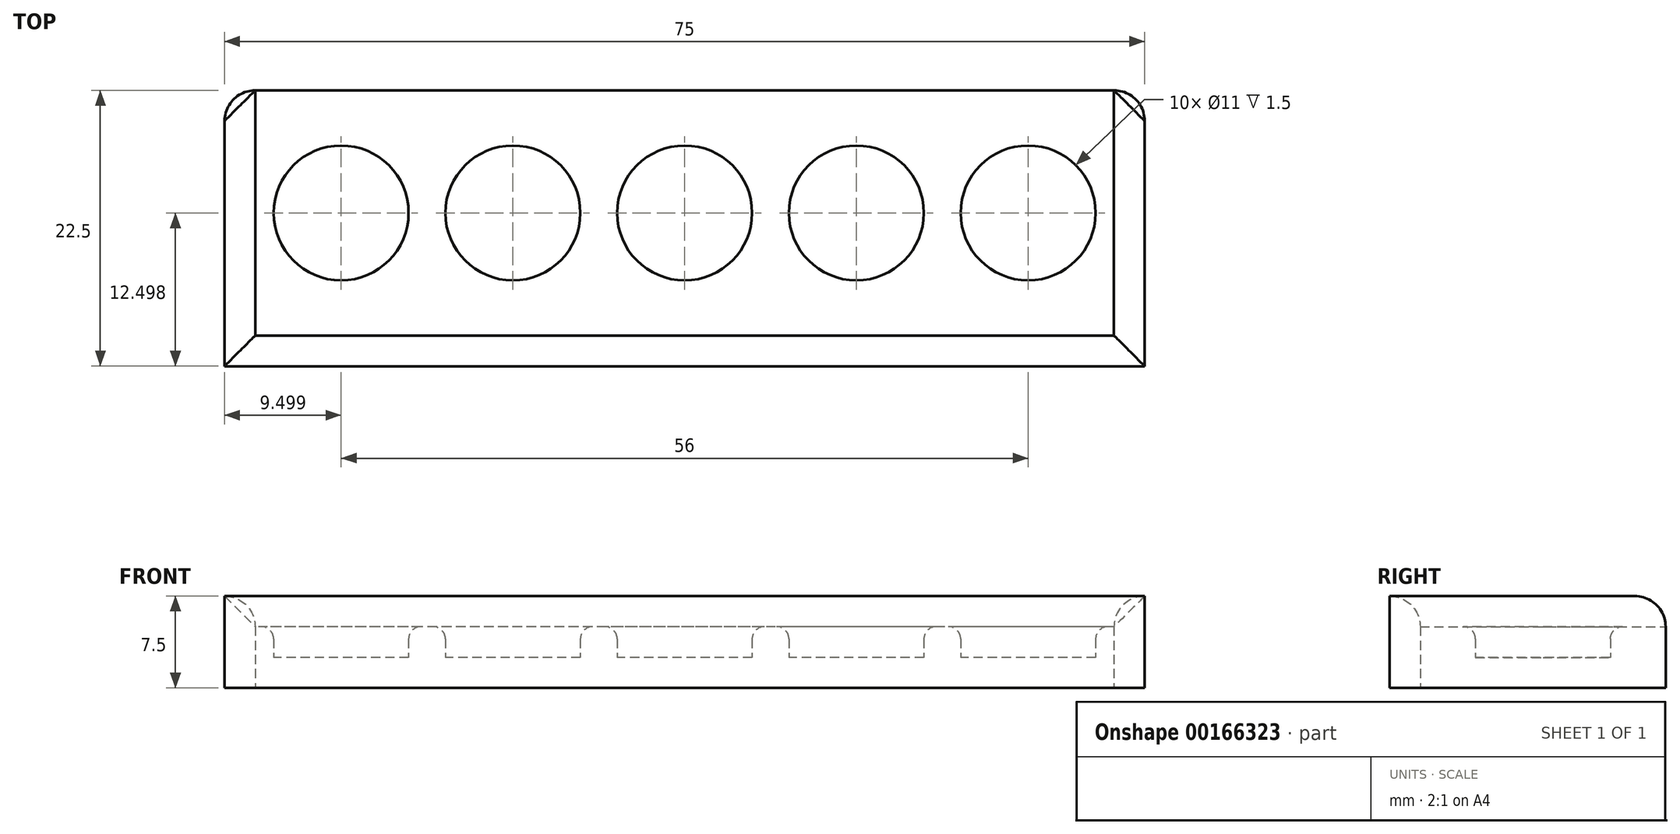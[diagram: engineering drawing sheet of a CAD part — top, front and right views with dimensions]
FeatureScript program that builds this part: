
annotation { "Feature Type Name" : "Feature", "Feature Type Description" : "" }
export const myFeature = defineFeature(function(context is Context, id is Id, definition is map)
    precondition{}
    {
        {
            var Q0;
            Q0=qCreatedBy(makeId("Top.planeOp"),FACE);
            var sketch = newSketch(context, id + "F0", { "sketchPlane" : qUnion([Q0])});
            skLineSegment(sketch, "E0.bottom", {"start": v(-145.22, 10.14) * mm, "end": v(-215.22, 10.14) * mm});
            skLineSegment(sketch, "E0.top", {"start": v(-145.22, 30.14) * mm, "end": v(-215.22, 30.14) * mm});
            skLineSegment(sketch, "E0.left", {"start": v(-145.22, 10.14) * mm, "end": v(-145.22, 30.14) * mm});
            skLineSegment(sketch, "E0.right", {"start": v(-215.22, 10.14) * mm, "end": v(-215.22, 30.14) * mm});
            skPoint(sketch, "E0.middle", {"position": v(-180.22, 20.14) * mm});
            skCircle(sketch, "E1", {"center": v(-180.22, 20.14) * mm, "radius": 5.5 * mm});
            skCircle(sketch, "E2", {"center": v(-166.22, 20.14) * mm, "radius": 5.5 * mm});
            skCircle(sketch, "E3", {"center": v(-152.22, 20.14) * mm, "radius": 5.5 * mm});
            skCircle(sketch, "E4", {"center": v(-194.22, 20.14) * mm, "radius": 5.5 * mm});
            skCircle(sketch, "E5", {"center": v(-208.22, 20.14) * mm, "radius": 5.5 * mm});
            skSolve(sketch);
        }
        {
            var Q0;
            Q0=makeQuery(id+"F0.imprint","IMPRINT",FACE,{"disambiguationData":[TD([[makeQuery(id+"F0.imprint","IMPRINT",EDGE,{"derivedFrom":sQuery(id+"F0.wireOp",EDGE,"E1")}),1.0]])]});
            var sketch = newSketch(context, id + "F1", { "sketchPlane" : qUnion([Q0])});
            skLineSegment(sketch, "E6.bottom", {"start": v(-145.22, 10.14) * mm, "end": v(-215.22, 10.14) * mm});
            skLineSegment(sketch, "E6.top", {"start": v(-145.22, 30.14) * mm, "end": v(-215.22, 30.14) * mm});
            skLineSegment(sketch, "E6.left", {"start": v(-145.22, 10.14) * mm, "end": v(-145.22, 30.14) * mm});
            skLineSegment(sketch, "E6.right", {"start": v(-215.22, 10.14) * mm, "end": v(-215.22, 30.14) * mm});
            skPoint(sketch, "E6.middle", {"position": v(-180.22, 20.14) * mm});
            skSolve(sketch);
        }
        {
            var Q0;
            Q0 = qSketchRegion(id + "F1", true);
            extrude(context, id + "F2", {"entities" : qUnion([Q0]), "depth" : 2.5 * mm, "hasSecondDirection" : true, "secondDirectionOppositeDirection" : true, "secondDirectionDepth" : 2.5 * mm});
        }
        {
            var Q0;
            Q0=makeQuery(id+"F0.imprint","IMPRINT",FACE,{"disambiguationData":[TD([[makeQuery(id+"F0.imprint","IMPRINT",EDGE,{"derivedFrom":sQuery(id+"F0.wireOp",EDGE,"E3")}),1.0]])]});
            var Q1;
            Q1=makeQuery(id+"F0.imprint","IMPRINT",FACE,{"disambiguationData":[TD([[makeQuery(id+"F0.imprint","IMPRINT",EDGE,{"derivedFrom":sQuery(id+"F0.wireOp",EDGE,"E2")}),1.0]])]});
            var Q2;
            Q2=makeQuery(id+"F0.imprint","IMPRINT",FACE,{"disambiguationData":[TD([[makeQuery(id+"F0.imprint","IMPRINT",EDGE,{"derivedFrom":sQuery(id+"F0.wireOp",EDGE,"E1")}),1.0]])]});
            var Q3;
            Q3=makeQuery(id+"F0.imprint","IMPRINT",FACE,{"disambiguationData":[TD([[makeQuery(id+"F0.imprint","IMPRINT",EDGE,{"derivedFrom":sQuery(id+"F0.wireOp",EDGE,"E4")}),1.0]])]});
            var Q4;
            Q4=makeQuery(id+"F0.imprint","IMPRINT",FACE,{"disambiguationData":[TD([[makeQuery(id+"F0.imprint","IMPRINT",EDGE,{"derivedFrom":sQuery(id+"F0.wireOp",EDGE,"E5")}),1.0]])]});
            extrude(context, id + "F3", {"entities" : qUnion([Q0, Q1, Q2, Q3, Q4]), "operationType" : NewBodyOperationType.REMOVE, "depth" : 25.4 * mm});
        }
        {
            var Q0;
            Q0=makeQuery(id+"F2.opExtrude","CAP_FACE",FACE,{"disambiguationData":[OSD([sQuery(id+"F1.wireOp",EDGE,"E6.bottom"),sQuery(id+"F1.wireOp",EDGE,"E6.top"),sQuery(id+"F1.wireOp",EDGE,"E6.left"),sQuery(id+"F1.wireOp",EDGE,"E6.right")])],"isStart":true});
            var sketch = newSketch(context, id + "F4", { "sketchPlane" : qUnion([Q0])});
            skLineSegment(sketch, "E7.bottom", {"start": v(-142.72, -30.14) * mm, "end": v(-217.72, -30.14) * mm});
            skLineSegment(sketch, "E7.top", {"start": v(-142.72, -7.64) * mm, "end": v(-217.72, -7.64) * mm});
            skLineSegment(sketch, "E7.left", {"start": v(-142.72, -30.14) * mm, "end": v(-142.72, -7.64) * mm});
            skLineSegment(sketch, "E7.right", {"start": v(-217.72, -30.14) * mm, "end": v(-217.72, -7.64) * mm});
            skSolve(sketch);
        }
        {
            var Q0;
            Q0=makeQuery(id+"F4.imprint","IMPRINT",FACE,{"disambiguationData":[TD([[makeQuery(id+"F4.imprint","IMPRINT",EDGE,{"derivedFrom":sQuery(id+"F4.wireOp",EDGE,"E7.top")}),1.0]])]});
            extrude(context, id + "F5", {"entities" : qUnion([Q0]), "oppositeDirection" : true, "depth" : 7.5 * mm});
        }
        {
            var Q0;
            Q0=makeQuery(id+"F5.opExtrude","CAP_EDGE",EDGE,{"disambiguationData":[OSD([sQuery(id+"F1.wireOp",EDGE,"E6.bottom")])],"isStart":false});
            var Q1;
            Q1=makeQuery(id+"F5.opExtrude","CAP_EDGE",EDGE,{"disambiguationData":[OSD([sQuery(id+"F1.wireOp",EDGE,"E6.left")])],"isStart":false});
            var Q2;
            Q2=makeQuery(id+"F5.opExtrude","CAP_EDGE",EDGE,{"disambiguationData":[OSD([sQuery(id+"F1.wireOp",EDGE,"E6.right")])],"isStart":false});
            var Q3;
            {var subQ0=sQuery(id+"F4.wireOp",EDGE,"E7.bottom");Q3=makeQuery(id+"F5.opExtrude","CAP_EDGE",EDGE,{"disambiguationData":[OSD([subQ0]),TDD([makeQuery(id+"F4.imprint","IMPRINT",EDGE,{"disambiguationData":[TD([[makeQuery(id+"F4.imprint","INTERSECT",VERTEX,{"derivedFrom":[makeQuery(id+"F2.opExtrude","CAP_EDGE",EDGE,{"disambiguationData":[OSD([sQuery(id+"F1.wireOp",EDGE,"E6.right")])],"isStart":true}),subQ0]}),-1.0]])],"derivedFrom":subQ0})])],"isStart":false});}
            var Q4;
            {var subQ0=sQuery(id+"F4.wireOp",EDGE,"E7.bottom");Q4=makeQuery(id+"F5.opExtrude","CAP_EDGE",EDGE,{"disambiguationData":[OSD([subQ0]),TDD([makeQuery(id+"F4.imprint","IMPRINT",EDGE,{"disambiguationData":[TD([[makeQuery(id+"F4.imprint","INTERSECT",VERTEX,{"derivedFrom":[makeQuery(id+"F2.opExtrude","CAP_EDGE",EDGE,{"disambiguationData":[OSD([sQuery(id+"F1.wireOp",EDGE,"E6.left")])],"isStart":true}),subQ0]}),1.0]])],"derivedFrom":subQ0})])],"isStart":false});}
            var Q5;
            Q5=makeQuery(id+"F5.opExtrude","SWEPT_EDGE",EDGE,{"disambiguationData":[OSD([sQuery(id+"F4.wireOp",EDGE,"E7.bottom"),sQuery(id+"F4.wireOp",EDGE,"E7.left")])]});
            var Q6;
            Q6=makeQuery(id+"F5.opExtrude","SWEPT_EDGE",EDGE,{"disambiguationData":[OSD([sQuery(id+"F4.wireOp",EDGE,"E7.bottom"),sQuery(id+"F4.wireOp",EDGE,"E7.right")])]});
            fillet(context, id + "F6", {"entities" : qUnion([Q0, Q1, Q2, Q3, Q4, Q5, Q6]), "radius" : 2.5 * mm, "tangentPropagation" : true, "allowEdgeOverflow" : false});
        }
        {
            var Q0;
            Q0=makeQuery(id+"F3.boolean.opBoolean","INTERSECT",EDGE,{"derivedFrom":[makeQuery(id+"F2.opExtrude","CAP_FACE",FACE,{"disambiguationData":[OSD([sQuery(id+"F1.wireOp",EDGE,"E6.bottom"),sQuery(id+"F1.wireOp",EDGE,"E6.top"),sQuery(id+"F1.wireOp",EDGE,"E6.left"),sQuery(id+"F1.wireOp",EDGE,"E6.right")])],"isStart":false}),makeQuery(id+"F3.opExtrude","SWEPT_FACE",FACE,{"disambiguationData":[OSD([sQuery(id+"F0.wireOp",EDGE,"E3")])]})]});
            var Q1;
            Q1=makeQuery(id+"F3.boolean.opBoolean","INTERSECT",EDGE,{"derivedFrom":[makeQuery(id+"F2.opExtrude","CAP_FACE",FACE,{"disambiguationData":[OSD([sQuery(id+"F1.wireOp",EDGE,"E6.bottom"),sQuery(id+"F1.wireOp",EDGE,"E6.top"),sQuery(id+"F1.wireOp",EDGE,"E6.left"),sQuery(id+"F1.wireOp",EDGE,"E6.right")])],"isStart":false}),makeQuery(id+"F3.opExtrude","SWEPT_FACE",FACE,{"disambiguationData":[OSD([sQuery(id+"F0.wireOp",EDGE,"E2")])]})]});
            var Q2;
            Q2=makeQuery(id+"F3.boolean.opBoolean","INTERSECT",EDGE,{"derivedFrom":[makeQuery(id+"F2.opExtrude","CAP_FACE",FACE,{"disambiguationData":[OSD([sQuery(id+"F1.wireOp",EDGE,"E6.bottom"),sQuery(id+"F1.wireOp",EDGE,"E6.top"),sQuery(id+"F1.wireOp",EDGE,"E6.left"),sQuery(id+"F1.wireOp",EDGE,"E6.right")])],"isStart":false}),makeQuery(id+"F3.opExtrude","SWEPT_FACE",FACE,{"disambiguationData":[OSD([sQuery(id+"F0.wireOp",EDGE,"E1")])]})]});
            var Q3;
            Q3=makeQuery(id+"F3.boolean.opBoolean","INTERSECT",EDGE,{"derivedFrom":[makeQuery(id+"F2.opExtrude","CAP_FACE",FACE,{"disambiguationData":[OSD([sQuery(id+"F1.wireOp",EDGE,"E6.bottom"),sQuery(id+"F1.wireOp",EDGE,"E6.top"),sQuery(id+"F1.wireOp",EDGE,"E6.left"),sQuery(id+"F1.wireOp",EDGE,"E6.right")])],"isStart":false}),makeQuery(id+"F3.opExtrude","SWEPT_FACE",FACE,{"disambiguationData":[OSD([sQuery(id+"F0.wireOp",EDGE,"E4")])]})]});
            var Q4;
            Q4=makeQuery(id+"F3.boolean.opBoolean","INTERSECT",EDGE,{"derivedFrom":[makeQuery(id+"F2.opExtrude","CAP_FACE",FACE,{"disambiguationData":[OSD([sQuery(id+"F1.wireOp",EDGE,"E6.bottom"),sQuery(id+"F1.wireOp",EDGE,"E6.top"),sQuery(id+"F1.wireOp",EDGE,"E6.left"),sQuery(id+"F1.wireOp",EDGE,"E6.right")])],"isStart":false}),makeQuery(id+"F3.opExtrude","SWEPT_FACE",FACE,{"disambiguationData":[OSD([sQuery(id+"F0.wireOp",EDGE,"E5")])]})]});
            fillet(context, id + "F7", {"entities" : qUnion([Q0, Q1, Q2, Q3, Q4]), "radius" : 1 * mm, "tangentPropagation" : true, "allowEdgeOverflow" : false});
        }
    });
